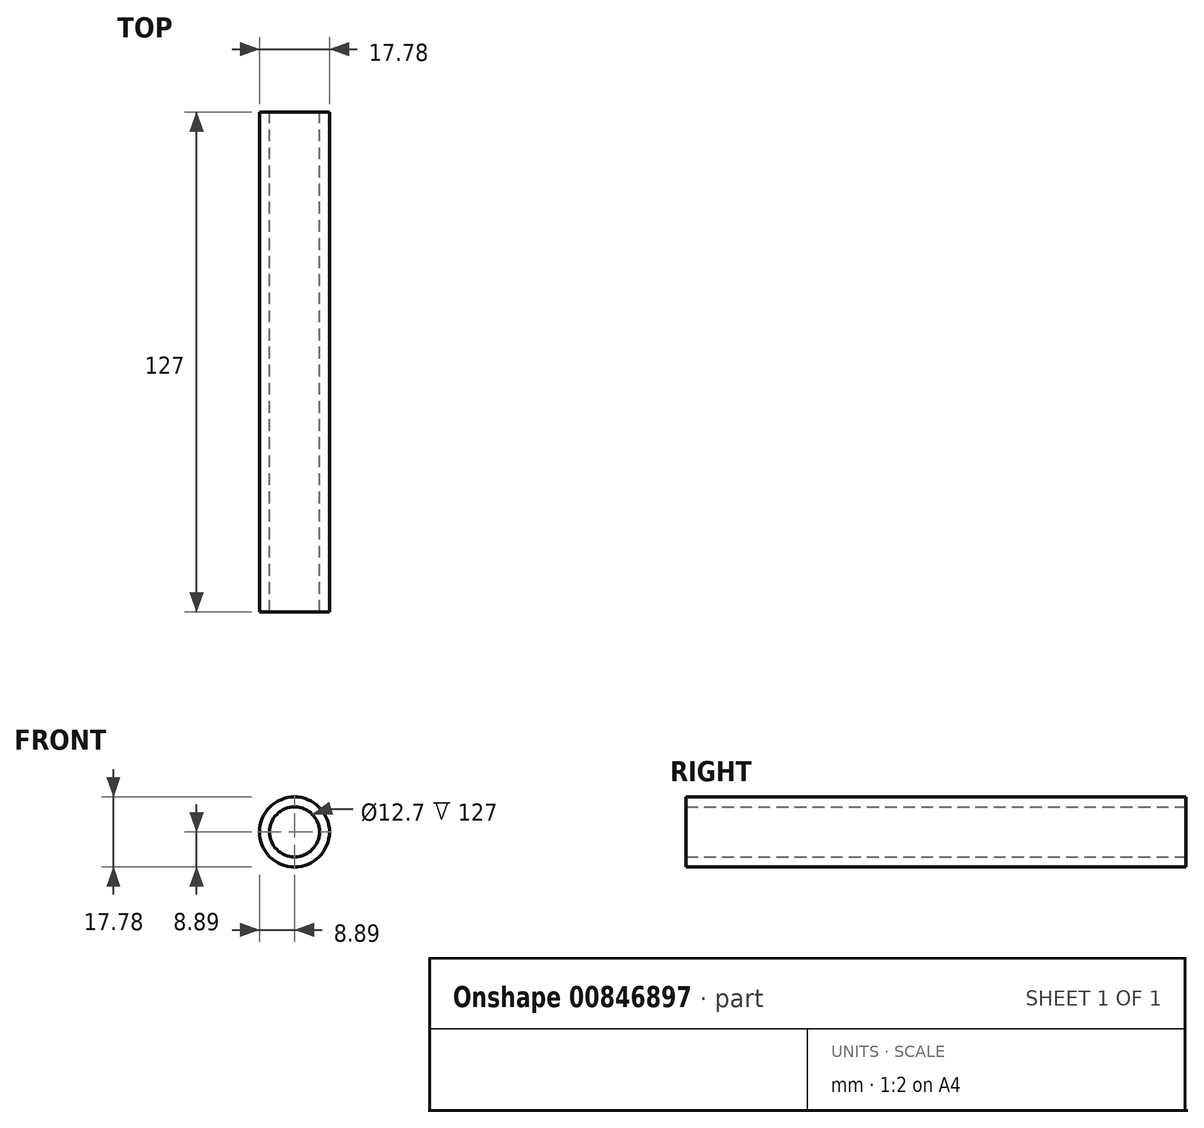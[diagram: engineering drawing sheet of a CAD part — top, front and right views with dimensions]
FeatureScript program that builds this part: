
annotation { "Feature Type Name" : "Feature", "Feature Type Description" : "" }
export const myFeature = defineFeature(function(context is Context, id is Id, definition is map)
    precondition{}
    {
        {
            var Q0;
            Q0=qCreatedBy(makeId("Front.planeOp"),FACE);
            var sketch = newSketch(context, id + "F0", { "sketchPlane" : qUnion([Q0])});
            skCircle(sketch, "E0", {"center": v(0, 0) * mm, "radius": 8.9 * mm});
            skCircle(sketch, "E1", {"center": v(0, 0) * mm, "radius": 6.35 * mm});
            skSolve(sketch);
        }
        {
            var Q0;
            Q0=makeQuery(id+"F0.imprint","IMPRINT",FACE,{"disambiguationData":[TD([[makeQuery(id+"F0.imprint","IMPRINT",EDGE,{"derivedFrom":sQuery(id+"F0.wireOp",EDGE,"E0")}),1.0]])]});
            extrude(context, id + "F1", {"entities" : qUnion([Q0]), "depth" : 127 * mm, "offsetDistance" : 25.4 * mm});
        }
    });
